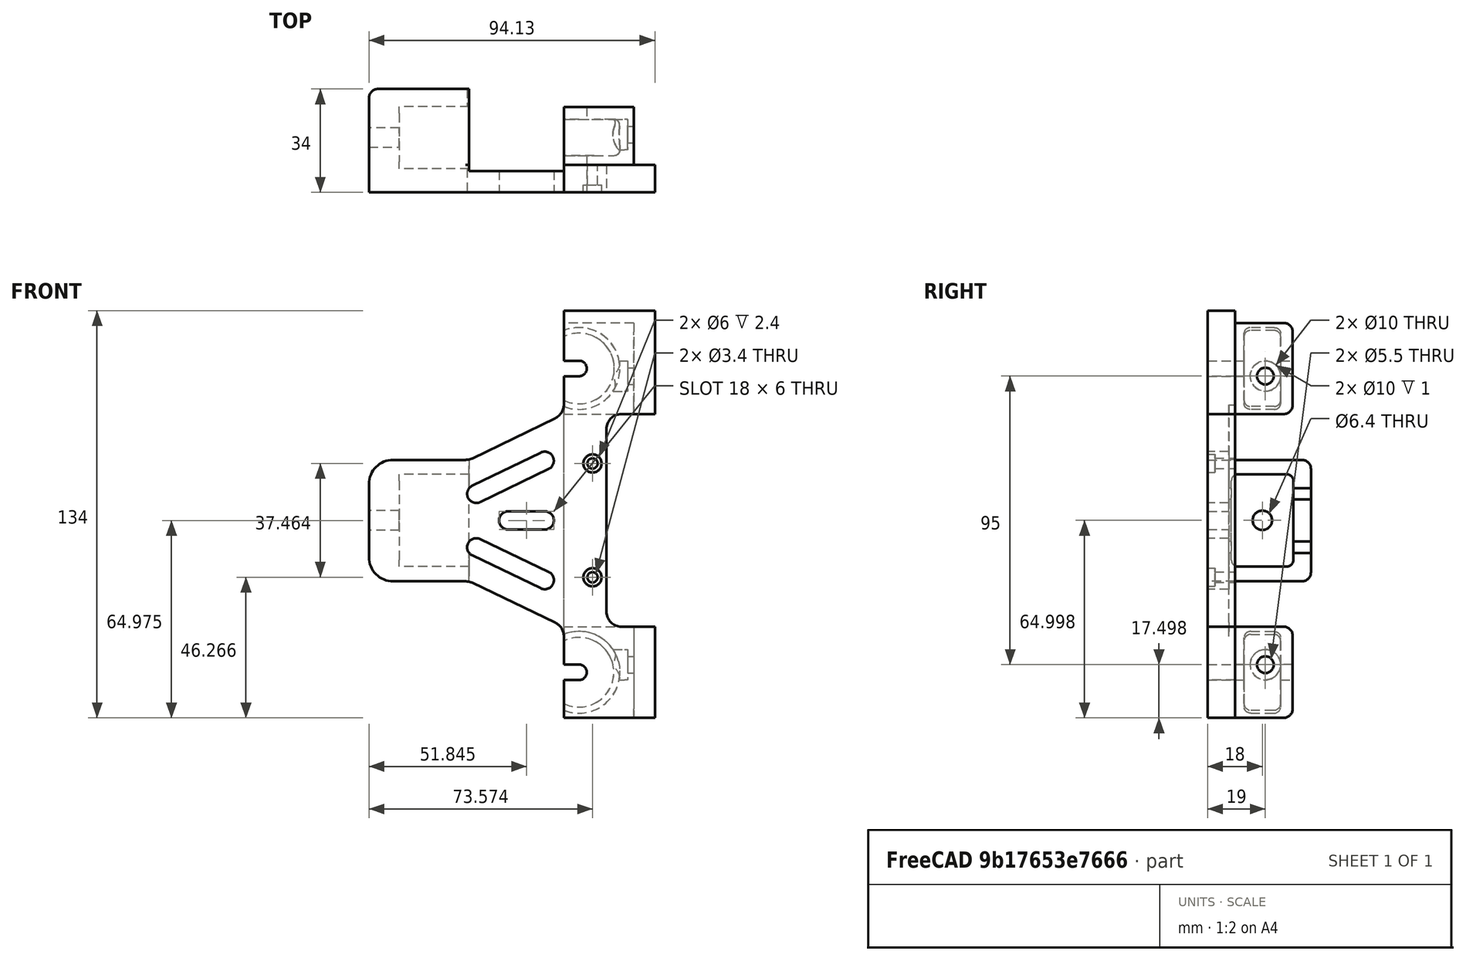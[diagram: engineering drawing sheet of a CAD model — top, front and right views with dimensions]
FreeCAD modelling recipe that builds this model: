
FCSTD DOCUMENT  (FreeCAD 0.20R29177 (Git))
Label: AQ_006a_VwheelZclamp
License: All rights reserved
LicenseURL: http://en.wikipedia.org/wiki/All_rights_reserved
objects: Sketcher::SketchObject×14, PartDesign::Pocket×9, PartDesign::Pad×5, PartDesign::Line×2, PartDesign::Groove×2, PartDesign::Hole×2, PartDesign::Fillet×2, PartDesign::SubShapeBinder×1, PartDesign::Body×1
note: 58 computed .brp shape members not serialized (recipe doc carries the construction recipe); baked Part::Feature solids carry a one-line shape summary decoded from their .brp

FEATURE [PartDesign::SubShapeBinder] Binder
  BindCopyOnChange = 0
  BindMode = 2
  ClaimChildren = false
  Context = -> Body [Binder.]
  Fuse = false
  MakeFace = true
  OffsetFill = false
  OffsetIntersection = false
  OffsetJoinType = 0
  OffsetOpenResult = false
  PartialLoad = false
  Relative = true
  _Version = 2
FEATURE [Sketcher::SketchObject] Sketch
  ExternalGeometry = -> [Binder]
  FullyConstrained = true
  MapMode = 5
  Placement = pos=(0,425,9.35e-14) rot=(1,0,0;1.5708rad)
  Support = -> [Binder]
  sketch-geometry (29):
    g0: LineSegment StartX=35.9712 StartY=288.702 StartZ=0 EndX=35.9712 EndY=315.568 EndZ=0
    g1: LineSegment StartX=35.9712 StartY=315.568 StartZ=0 EndX=58.9712 EndY=315.568 EndZ=0
    g2: LineSegment StartX=58.9712 StartY=315.568 StartZ=0 EndX=58.9712 EndY=285.568 EndZ=0
    g3: LineSegment StartX=58.9712 StartY=185.568 StartZ=0 EndX=35.9712 EndY=185.568 EndZ=0
    g4: LineSegment StartX=35.9712 StartY=185.568 StartZ=0 EndX=35.9712 EndY=212.42 EndZ=0
    g5: LineSegment StartX=58.9712 StartY=215.568 StartZ=0 EndX=58.9712 EndY=185.568 EndZ=0
    g6: LineSegment StartX=5.87245 StartY=270.987 StartZ=0 EndX=33.1511 EndY=284.202 EndZ=0
    g7: LineSegment StartX=5.86449 StartY=229.996 StartZ=0 EndX=33.1319 EndY=216.929 EndZ=0
    g8: LineSegment StartX=58.9712 StartY=285.568 StartZ=0 EndX=54.9712 EndY=285.568 EndZ=0
    g9: LineSegment StartX=49.9712 StartY=285.568 StartZ=0 EndX=35.9712 EndY=285.568 EndZ=0
    g10: LineSegment StartX=35.9712 StartY=215.568 StartZ=0 EndX=49.9712 EndY=215.568 EndZ=0
    g11: LineSegment StartX=54.9712 StartY=215.568 StartZ=0 EndX=58.9712 EndY=215.568 EndZ=0
    g12: LineSegment StartX=49.9712 StartY=280.568 StartZ=0 EndX=49.9712 EndY=220.568 EndZ=0
    g13: ArcOfCircle CenterX=54.9712 CenterY=280.568 CenterZ=0 NormalX=0 NormalY=0 NormalZ=1 AngleXU=0 Radius=5 StartAngle=1.5708 EndAngle=3.14159
    g14: GeomPoint X=49.9712 Y=285.568 Z=0
    g15: ArcOfCircle CenterX=54.9712 CenterY=220.568 CenterZ=0 NormalX=0 NormalY=0 NormalZ=1 AngleXU=0 Radius=5 StartAngle=3.14159 EndAngle=4.71239
    g16: GeomPoint X=49.9712 Y=215.568 Z=0
    g17: ArcOfCircle CenterX=30.9712 CenterY=288.702 CenterZ=0 NormalX=0 NormalY=0 NormalZ=1 AngleXU=0 Radius=5 StartAngle=5.16352 EndAngle=6.28319
    g18: GeomPoint X=35.9712 Y=285.568 Z=0
    g19: ArcOfCircle CenterX=30.9712 CenterY=212.42 CenterZ=0 NormalX=0 NormalY=0 NormalZ=1 AngleXU=0 Radius=5 StartAngle=-1.8e-15 EndAngle=1.12392
    g20: GeomPoint X=35.9712 Y=215.568 Z=0
    g21: LineSegment StartX=-28.1601 StartY=270.487 StartZ=0 EndX=3.69255 EndY=270.487 EndZ=0
    g22: LineSegment StartX=4.83989 StartY=270.487 StartZ=0 EndX=4.83989 EndY=230.487 EndZ=0
    g23: LineSegment StartX=3.70372 StartY=230.487 StartZ=0 EndX=-28.1601 EndY=230.487 EndZ=0
    g24: LineSegment StartX=-28.1601 StartY=230.487 StartZ=0 EndX=-28.1601 EndY=270.487 EndZ=0
    g25: ArcOfCircle CenterX=3.70372 CenterY=225.487 CenterZ=0 NormalX=0 NormalY=0 NormalZ=1 AngleXU=0 Radius=5 StartAngle=1.12392 EndAngle=1.5708
    g26: GeomPoint X=4.83989 Y=230.487 Z=0
    g27: ArcOfCircle CenterX=3.69255 CenterY=275.487 CenterZ=0 NormalX=0 NormalY=0 NormalZ=1 AngleXU=0 Radius=5 StartAngle=4.71239 EndAngle=5.16352
    g28: GeomPoint X=4.83989 Y=270.487 Z=0
  constraints (68):
    c: Coincident(g9,g18)
    c: Coincident(g0,g1)
    c: Coincident(g1,g2)
    c: Coincident(g2,g8)
    c: Horizontal(g1)
    c: Vertical(g0)
    c: Vertical(g2)
    c: Coincident(g8,g-4)
    c: Coincident(g0,g-3)
    c: Coincident(g3,g4)
    c: Coincident(g20,g10)
    c: Coincident(g11,g5)
    c: Coincident(g5,g3)
    c: Horizontal(g3)
    c: Vertical(g4)
    c: Vertical(g5)
    c: Coincident(g3,g-9)
    c: Coincident(g20,g-8)
    c: Coincident(g14,g9)
    c: Horizontal(g8)
    c: Horizontal(g9)
    c: Coincident(g10,g16)
    c: Horizontal(g10)
    c: Horizontal(g11)
    c: Vertical(g12)
    c: DistanceX(g14,g8) = 9
    c: PointOnObject(g14,g12)
    c: PointOnObject(g14,g8)
    c: Tangent(g12,g13) = -1.5708
    c: Tangent(g8,g13) = -1.5708
    c: PointOnObject(g16,g11)
    c: PointOnObject(g16,g12)
    c: Tangent(g11,g15) = -1.5708
    c: Tangent(g12,g15) = -1.5708
    c: PointOnObject(g18,g6)
    c: PointOnObject(g18,g0)
    c: Tangent(g6,g17) = -1.5708
    c: Tangent(g0,g17) = -1.5708
    c: PointOnObject(g20,g7)
    c: PointOnObject(g20,g4)
    c: Tangent(g7,g19) = 1.5708
    c: Tangent(g4,g19) = -1.5708
    c: Equal(g17,g19)
    c: Equal(g19,g15)
    c: Equal(g15,g13)
    c: Radius(g13) = 5
    c: Coincident(g28,g22)
    c: Coincident(g22,g26)
    c: Coincident(g23,g24)
    c: Coincident(g24,g21)
    c: Horizontal(g21)
    c: Horizontal(g23)
    c: Vertical(g22)
    c: Vertical(g24)
    c: DistanceY(g-10,g21) = 5
    c: DistanceX(g21,g-10) = 10
    c: DistanceY(g23,g-11) = 5
    c: PointOnObject(g26,g23)
    c: PointOnObject(g26,g7)
    c: Tangent(g23,g25) = -1.5708
    c: Tangent(g7,g25) = 1.5708
    c: PointOnObject(g28,g21)
    c: PointOnObject(g28,g6)
    c: Tangent(g21,g27) = -1.5708
    c: Tangent(g6,g27) = -1.5708
    c: Equal(g27,g25)
    c: Equal(g25,g19)
    c: Vertical(g22,g-10)
FEATURE [PartDesign::Pad] Pad
  Direction = (0,-1,-2e-16)
  Length = 9
  Length2 = 10
  Profile = -> Sketch
  ReferenceAxis = -> Sketch [N_Axis]
  Type = 0
FEATURE [Sketcher::SketchObject] Sketch001
  ExternalGeometry = -> [Pad,Binder]
  FullyConstrained = true
  MapMode = 5
  Placement = pos=(0,425,0) rot=(0,0.707107,0.707107;3.14159rad)
  Support = -> [Pad]
  sketch-geometry (4):
    g0: LineSegment StartX=28.1601 StartY=230.487 StartZ=0 EndX=-4.83989 EndY=230.487 EndZ=0
    g1: LineSegment StartX=-4.83989 StartY=230.487 StartZ=0 EndX=-4.83989 EndY=270.487 EndZ=0
    g2: LineSegment StartX=-4.83989 StartY=270.487 StartZ=0 EndX=28.1601 EndY=270.487 EndZ=0
    g3: LineSegment StartX=28.1601 StartY=270.487 StartZ=0 EndX=28.1601 EndY=230.487 EndZ=0
  constraints (10):
    c: Coincident(g0,g1)
    c: Coincident(g1,g2)
    c: Coincident(g2,g3)
    c: Coincident(g3,g0)
    c: Horizontal(g0)
    c: Horizontal(g2)
    c: Vertical(g1)
    c: Coincident(g0,g-3)
    c: Coincident(g2,g-3)
    c: Vertical(g1,g-4)
FEATURE [PartDesign::Pad] Pad001
  BaseFeature = -> Pad
  Direction = (0,1,-2e-16)
  Length = 25
  Length2 = 10
  Profile = -> Sketch001
  ReferenceAxis = -> Sketch001 [N_Axis]
  Type = 0
FEATURE [Sketcher::SketchObject] Sketch002
  ExternalGeometry = -> [Binder]
  FullyConstrained = true
  MapMode = 5
  Placement = pos=(4.83989,0,0) rot=(0.57735,0.57735,0.57735;2.0944rad)
  Support = -> [Pad001]
  sketch-geometry (10):
    g0: ArcOfCircle CenterX=426 CenterY=237.568 CenterZ=0 NormalX=0 NormalY=0 NormalZ=1 AngleXU=0 Radius=2.2 StartAngle=3.14159 EndAngle=4.71239
    g1: LineSegment StartX=423.8 StartY=237.568 StartZ=0 EndX=423.8 EndY=263.568 EndZ=0
    g2: ArcOfCircle CenterX=426 CenterY=263.568 CenterZ=0 NormalX=0 NormalY=0 NormalZ=1 AngleXU=0 Radius=2.2 StartAngle=1.5708 EndAngle=3.14159
    g3: LineSegment StartX=426 StartY=265.768 StartZ=0 EndX=442 EndY=265.768 EndZ=0
    g4: ArcOfCircle CenterX=442 CenterY=263.568 CenterZ=0 NormalX=0 NormalY=0 NormalZ=1 AngleXU=0 Radius=2.2 StartAngle=9e-16 EndAngle=1.5708
    g5: LineSegment StartX=444.2 StartY=263.568 StartZ=0 EndX=444.2 EndY=237.568 EndZ=0
    g6: ArcOfCircle CenterX=442 CenterY=237.568 CenterZ=0 NormalX=0 NormalY=0 NormalZ=1 AngleXU=0 Radius=2.2 StartAngle=4.71239 EndAngle=6.28319
    g7: LineSegment StartX=442 StartY=235.368 StartZ=0 EndX=426 EndY=235.368 EndZ=0
    g8: GeomPoint X=423.8 Y=235.368 Z=0
    g9: GeomPoint X=444.2 Y=265.768 Z=0
  constraints (22):
    c: Tangent(g0,g1) = 1.5708
    c: Tangent(g1,g2) = 1.5708
    c: Tangent(g2,g3) = 1.5708
    c: Tangent(g3,g4) = 1.5708
    c: Tangent(g4,g5) = 1.5708
    c: Tangent(g5,g6) = 1.5708
    c: Tangent(g6,g7) = 1.5708
    c: Tangent(g7,g0) = 1.5708
    c: Horizontal(g3)
    c: Horizontal(g7)
    c: Vertical(g1)
    c: Vertical(g5)
    c: Equal(g0,g2)
    c: Equal(g2,g4)
    c: Equal(g4,g6)
    c: PointOnObject(g8,g1)
    c: PointOnObject(g8,g7)
    c: PointOnObject(g9,g3)
    c: PointOnObject(g9,g5)
    c: Coincident(g0,g-4)
    c: Coincident(g4,g-3)
    c: DistanceX(g-3,g4) = 0.2
FEATURE [PartDesign::Pocket] Pocket
  BaseFeature = -> Pad001
  Direction = (-1,0,0)
  Length = 23
  Length2 = 5
  Profile = -> Sketch002
  ReferenceAxis = -> Sketch002 [N_Axis]
  Type = 0
FEATURE [Sketcher::SketchObject] Sketch003
  ExternalGeometry = -> [Pocket]
  FullyConstrained = true
  MapMode = 5
  Placement = pos=(-28.1601,0,0) rot=(0.57735,-0.57735,-0.57735;2.0944rad)
  Support = -> [Pocket]
  sketch-geometry (1):
    g0: Circle CenterX=-434 CenterY=250.568 CenterZ=0 NormalX=0 NormalY=0 NormalZ=1 AngleXU=0 Radius=3.2
  constraints (2):
    c: Symmetric(g-4,g-3,g0)
    c: Radius(g0) = 3.2
FEATURE [PartDesign::Pocket] Pocket001
  BaseFeature = -> Pocket
  Direction = (1,0,0)
  Length = 5
  Length2 = 5
  Profile = -> Sketch003
  ReferenceAxis = -> Sketch003 [N_Axis]
  Type = 1
FEATURE [Sketcher::SketchObject] Sketch004
  ExternalGeometry = -> [Pocket001]
  FullyConstrained = true
  MapMode = 5
  Placement = pos=(0,425,0) rot=(0,0.707107,0.707107;3.14159rad)
  Support = -> [Pocket001]
  sketch-geometry (8):
    g0: LineSegment StartX=-58.9712 StartY=315.568 StartZ=0 EndX=-35.9712 EndY=315.568 EndZ=0
    g1: LineSegment StartX=-35.9712 StartY=315.568 StartZ=0 EndX=-35.9712 EndY=285.568 EndZ=0
    g2: LineSegment StartX=-35.9712 StartY=285.568 StartZ=0 EndX=-58.9712 EndY=285.568 EndZ=0
    g3: LineSegment StartX=-58.9712 StartY=285.568 StartZ=0 EndX=-58.9712 EndY=315.568 EndZ=0
    g4: LineSegment StartX=-58.9712 StartY=185.568 StartZ=0 EndX=-35.9712 EndY=185.568 EndZ=0
    g5: LineSegment StartX=-35.9712 StartY=185.568 StartZ=0 EndX=-35.9712 EndY=215.568 EndZ=0
    g6: LineSegment StartX=-35.9712 StartY=215.568 StartZ=0 EndX=-58.9712 EndY=215.568 EndZ=0
    g7: LineSegment StartX=-58.9712 StartY=215.568 StartZ=0 EndX=-58.9712 EndY=185.568 EndZ=0
  constraints (18):
    c: Coincident(g0,g1)
    c: Coincident(g1,g2)
    c: Coincident(g2,g3)
    c: Coincident(g3,g0)
    c: Horizontal(g2)
    c: Vertical(g1)
    c: Coincident(g0,g-3)
    c: Coincident(g4,g5)
    c: Coincident(g5,g6)
    c: Coincident(g6,g7)
    c: Coincident(g7,g4)
    c: Horizontal(g6)
    c: Vertical(g5)
    c: Coincident(g4,g-4)
    c: Coincident(g4,g-6)
    c: Coincident(g6,g-4)
    c: Coincident(g2,g-3)
    c: Coincident(g0,g-5)
FEATURE [PartDesign::Pad] Pad002
  BaseFeature = -> Pocket001
  Direction = (0,1,-2e-16)
  Length = 19
  Length2 = 10
  Profile = -> Sketch004
  ReferenceAxis = -> Sketch004 [N_Axis]
  Type = 0
FEATURE [Sketcher::SketchObject] Sketch005
  ExternalGeometry = -> [Binder]
  FullyConstrained = false
  MapMode = 5
  Placement = pos=(0,416,0) rot=(1,0,0;1.5708rad)
  Support = -> [Pad002]
  sketch-geometry (8):
    g0: ArcOfCircle CenterX=40.9712 CenterY=300.568 CenterZ=0 NormalX=0 NormalY=0 NormalZ=1 AngleXU=0 Radius=2.55 StartAngle=4.71239 EndAngle=7.85398
    g1: ArcOfCircle CenterX=28.0558 CenterY=300.568 CenterZ=0 NormalX=0 NormalY=0 NormalZ=1 AngleXU=0 Radius=2.55 StartAngle=1.5708 EndAngle=4.71239
    g2: LineSegment StartX=40.9712 StartY=303.118 StartZ=0 EndX=28.0558 EndY=303.118 EndZ=0
    g3: LineSegment StartX=28.0558 StartY=298.018 StartZ=0 EndX=40.9712 EndY=298.018 EndZ=0
    g4: ArcOfCircle CenterX=40.9712 CenterY=200.568 CenterZ=0 NormalX=0 NormalY=0 NormalZ=1 AngleXU=0 Radius=2.55 StartAngle=4.71239 EndAngle=7.85398
    g5: ArcOfCircle CenterX=29.0578 CenterY=200.568 CenterZ=0 NormalX=0 NormalY=0 NormalZ=1 AngleXU=0 Radius=2.55 StartAngle=1.5708 EndAngle=4.71239
    g6: LineSegment StartX=40.9712 StartY=203.118 StartZ=0 EndX=29.0578 EndY=203.118 EndZ=0
    g7: LineSegment StartX=29.0578 StartY=198.018 StartZ=0 EndX=40.9712 EndY=198.018 EndZ=0
  constraints (16):
    c: Tangent(g0,g2) = -1.5708
    c: Tangent(g2,g1) = -1.5708
    c: Tangent(g1,g3) = -1.5708
    c: Tangent(g3,g0) = -1.5708
    c: Equal(g0,g1)
    c: Coincident(g0,g-3)
    c: Horizontal(g2)
    c: Equal(g0,g-3)
    c: Tangent(g4,g6) = -1.5708
    c: Tangent(g6,g5) = -1.5708
    c: Tangent(g5,g7) = -1.5708
    c: Tangent(g7,g4) = -1.5708
    c: Equal(g4,g5)
    c: Coincident(g4,g-4)
    c: Horizontal(g6)
    c: Equal(g4,g-4)
FEATURE [PartDesign::Pocket] Pocket002
  BaseFeature = -> Pad002
  Direction = (0,1,-2e-16)
  Length = 5
  Length2 = 5
  Profile = -> Sketch005
  ReferenceAxis = -> Sketch005 [N_Axis]
  Type = 1
FEATURE [PartDesign::Line] DatumLine
  AttacherType = Attacher::AttachEngineLine
  Length = 20
  MapMode = 19
  Placement = pos=(40.9712,416,300.568) rot=(-0.57735,-0.57735,0.57735;4.18879rad)
  ResizeMode = 0
  Support = -> [Pocket002]
FEATURE [PartDesign::Line] DatumLine001
  AttacherType = Attacher::AttachEngineLine
  Length = 20
  MapMode = 19
  Placement = pos=(40.9712,416,200.568) rot=(-0.57735,-0.57735,0.57735;4.18879rad)
  ResizeMode = 0
  Support = -> [Pocket002]
FEATURE [Sketcher::SketchObject] Sketch006
  ExternalGeometry = -> [Binder,DatumLine]
  FullyConstrained = false
  MapMode = 5
  Placement = pos=(35.9712,0,0) rot=(0.57735,-0.57735,-0.57735;2.0944rad)
  Support = -> [Pocket002]
  sketch-geometry (8):
    g0: LineSegment StartX=-428 StartY=300.568 StartZ=0 EndX=-440 EndY=300.568 EndZ=0
    g1: LineSegment StartX=-440 StartY=300.568 StartZ=0 EndX=-440 EndY=311.056 EndZ=0
    g2: LineSegment StartX=-438.001 StartY=313.054 StartZ=0 EndX=-429.999 EndY=313.054 EndZ=0
    g3: LineSegment StartX=-428 StartY=311.056 StartZ=0 EndX=-428 EndY=300.568 EndZ=0
    g4: ArcOfCircle CenterX=-438.001 CenterY=311.056 CenterZ=0 NormalX=0 NormalY=0 NormalZ=1 AngleXU=0 Radius=1.99862 StartAngle=1.5708 EndAngle=3.14159
    g5: GeomPoint X=-440 Y=313.054 Z=0
    g6: ArcOfCircle CenterX=-429.999 CenterY=311.056 CenterZ=0 NormalX=0 NormalY=0 NormalZ=1 AngleXU=0 Radius=1.99862 StartAngle=1.13e-14 EndAngle=1.5708
    g7: GeomPoint X=-428 Y=313.054 Z=0
  constraints (19):
    c: Coincident(g0,g1)
    c: Coincident(g3,g0)
    c: Horizontal(g0)
    c: Horizontal(g2)
    c: Vertical(g1)
    c: Vertical(g3)
    c: PointOnObject(g0,g-5)
    c: Horizontal(g5,g-6)
    c: Vertical(g5,g-4)
    c: Vertical(g7,g-3)
    c: PointOnObject(g5,g1)
    c: PointOnObject(g5,g2)
    c: Tangent(g1,g4) = 1.5708
    c: Tangent(g2,g4) = 1.5708
    c: PointOnObject(g7,g2)
    c: PointOnObject(g7,g3)
    c: Tangent(g2,g6) = 1.5708
    c: Tangent(g3,g6) = 1.5708
    c: Equal(g4,g6)
FEATURE [PartDesign::Groove] Groove
  Angle = 360
  Axis = (-3e-16,-1,3e-16)
  Base = (40.9712,416,300.568)
  BaseFeature = -> Pocket002
  Profile = -> Sketch006
  ReferenceAxis = -> DatumLine
  Reversed = true
FEATURE [Sketcher::SketchObject] Sketch007
  ExternalGeometry = -> [DatumLine001,Binder]
  FullyConstrained = false
  MapMode = 5
  Placement = pos=(35.9712,0,0) rot=(0.57735,-0.57735,-0.57735;2.0944rad)
  Support = -> [Groove]
  sketch-geometry (8):
    g0: LineSegment StartX=-440 StartY=200.568 StartZ=0 EndX=-428 EndY=200.568 EndZ=0
    g1: LineSegment StartX=-428 StartY=200.568 StartZ=0 EndX=-428 EndY=190.264 EndZ=0
    g2: LineSegment StartX=-430.182 StartY=188.082 StartZ=0 EndX=-437.818 EndY=188.082 EndZ=0
    g3: LineSegment StartX=-440 StartY=190.264 StartZ=0 EndX=-440 EndY=200.568 EndZ=0
    g4: ArcOfCircle CenterX=-430.182 CenterY=190.264 CenterZ=0 NormalX=0 NormalY=0 NormalZ=1 AngleXU=0 Radius=2.18218 StartAngle=4.71239 EndAngle=6.28319
    g5: GeomPoint X=-428 Y=188.082 Z=0
    g6: ArcOfCircle CenterX=-437.818 CenterY=190.264 CenterZ=0 NormalX=0 NormalY=0 NormalZ=1 AngleXU=0 Radius=2.18218 StartAngle=3.14159 EndAngle=4.71239
    g7: GeomPoint X=-440 Y=188.082 Z=0
  constraints (18):
    c: Coincident(g0,g1)
    c: Coincident(g3,g0)
    c: Horizontal(g0)
    c: Vertical(g1)
    c: Vertical(g3)
    c: PointOnObject(g0,g-3)
    c: PointOnObject(g-10,g1)
    c: PointOnObject(g-13,g3)
    c: Tangent(g2,g-11)
    c: PointOnObject(g5,g2)
    c: PointOnObject(g5,g1)
    c: Tangent(g2,g4) = 1.5708
    c: Tangent(g1,g4) = 1.5708
    c: PointOnObject(g7,g2)
    c: PointOnObject(g7,g3)
    c: Tangent(g2,g6) = 1.5708
    c: Tangent(g3,g6) = 1.5708
    c: Equal(g6,g4)
FEATURE [PartDesign::Groove] Groove001
  Angle = 360
  Axis = (-2e-16,-1,3e-16)
  Base = (40.9712,416,200.568)
  BaseFeature = -> Groove
  Profile = -> Sketch007
  ReferenceAxis = -> DatumLine001
  Reversed = true
FEATURE [Sketcher::SketchObject] Sketch008
  AttachmentOffset = pos=(0,0,-16) rot=(0,0,1;0rad)
  ExternalGeometry = -> [Binder]
  FullyConstrained = false
  MapMode = 5
  Placement = pos=(51.9712,0,0) rot=(0.57735,-0.57735,-0.57735;2.0944rad)
  Support = -> [Groove001]
  sketch-geometry (2):
    g0: Circle CenterX=-435 CenterY=203.068 CenterZ=0 NormalX=0 NormalY=0 NormalZ=1 AngleXU=0 Radius=3.5552
    g1: Circle CenterX=-435 CenterY=298.068 CenterZ=0 NormalX=0 NormalY=0 NormalZ=1 AngleXU=0 Radius=4.0073
  constraints (2):
    c: Coincident(g0,g-4)
    c: Coincident(g1,g-3)
FEATURE [Sketcher::SketchObject] Sketch009
  ExternalGeometry = -> [Groove001]
  FullyConstrained = true
  MapMode = 5
  Placement = pos=(35.9712,0,0) rot=(0.57735,-0.57735,-0.57735;2.0944rad)
  Support = -> [Groove001]
  sketch-geometry (4):
    g0: LineSegment StartX=-440 StartY=290.081 StartZ=0 EndX=-428 EndY=290.081 EndZ=0
    g1: LineSegment StartX=-428 StartY=290.081 StartZ=0 EndX=-428 EndY=311.056 EndZ=0
    g2: LineSegment StartX=-428 StartY=311.056 StartZ=0 EndX=-440 EndY=311.056 EndZ=0
    g3: LineSegment StartX=-440 StartY=311.056 StartZ=0 EndX=-440 EndY=290.081 EndZ=0
  constraints (10):
    c: Coincident(g0,g1)
    c: Coincident(g1,g2)
    c: Coincident(g2,g3)
    c: Coincident(g3,g0)
    c: Horizontal(g0)
    c: Horizontal(g2)
    c: Vertical(g1)
    c: Vertical(g3)
    c: Coincident(g0,g-4)
    c: Coincident(g1,g-3)
FEATURE [PartDesign::Pocket] Pocket003
  BaseFeature = -> Groove001
  Direction = (1,0,0)
  Length = 10
  Length2 = 5
  Profile = -> Sketch009
  ReferenceAxis = -> Sketch009 [N_Axis]
  Type = 0
FEATURE [Sketcher::SketchObject] Sketch010
  ExternalGeometry = -> [Pocket003]
  FullyConstrained = true
  MapMode = 5
  Placement = pos=(35.9712,0,0) rot=(0.57735,-0.57735,-0.57735;2.0944rad)
  Support = -> [Pocket003]
  sketch-geometry (4):
    g0: LineSegment StartX=-440 StartY=190.264 StartZ=0 EndX=-428 EndY=190.264 EndZ=0
    g1: LineSegment StartX=-428 StartY=190.264 StartZ=0 EndX=-428 EndY=210.872 EndZ=0
    g2: LineSegment StartX=-428 StartY=210.872 StartZ=0 EndX=-440 EndY=210.872 EndZ=0
    g3: LineSegment StartX=-440 StartY=210.872 StartZ=0 EndX=-440 EndY=190.264 EndZ=0
  constraints (10):
    c: Coincident(g0,g1)
    c: Coincident(g1,g2)
    c: Coincident(g2,g3)
    c: Coincident(g3,g0)
    c: Horizontal(g0)
    c: Horizontal(g2)
    c: Vertical(g1)
    c: Vertical(g3)
    c: Coincident(g0,g-4)
    c: Coincident(g1,g-3)
FEATURE [PartDesign::Pocket] Pocket004
  BaseFeature = -> Pocket003
  Direction = (1,0,0)
  Length = 10
  Length2 = 5
  Profile = -> Sketch010
  ReferenceAxis = -> Sketch010 [N_Axis]
  Type = 0
FEATURE [PartDesign::Hole] Hole
  BaseFeature = -> Pocket004
  CustomThreadClearance = 0
  Depth = 25
  DepthType = 0
  Diameter = 5.5
  DrillForDepth = false
  DrillPoint = 1
  DrillPointAngle = 118
  HoleCutCountersinkAngle = 90
  HoleCutCustomValues = false
  HoleCutDepth = 4
  HoleCutDiameter = 10
  HoleCutType = 6
  ModelThread = false
  Profile = -> Sketch008
  Tapered = false
  TaperedAngle = 90
  ThreadClass = 0
  ThreadDepth = 25
  ThreadDepthType = 0
  ThreadDirection = 0
  ThreadFit = 0
  ThreadSize = 13
  ThreadType = 1
  Threaded = false
  UseCustomThreadClearance = false
FEATURE [PartDesign::Pocket] Pocket005
  BaseFeature = -> Hole
  Direction = (1,0,0)
  Length = 1
  Length2 = 5
  Profile = -> Hole [Face101]
  Type = 0
FEATURE [PartDesign::Pocket] Pocket006
  BaseFeature = -> Pocket005
  Direction = (1,0,0)
  Length = 1
  Length2 = 5
  Profile = -> Pocket005 [Face100]
  Type = 0
FEATURE [Sketcher::SketchObject] Sketch011
  ExternalGeometry = -> [Binder]
  FullyConstrained = false
  MapMode = 5
  Placement = pos=(0,416,0) rot=(1,0,0;1.5708rad)
  Support = -> [Pocket006]
  sketch-geometry (2):
    g0: Circle CenterX=45.4137 CenterY=269.3 CenterZ=0 NormalX=0 NormalY=0 NormalZ=1 AngleXU=0 Radius=4.58581
    g1: Circle CenterX=45.4137 CenterY=231.836 CenterZ=0 NormalX=0 NormalY=0 NormalZ=1 AngleXU=0 Radius=3.59318
  constraints (2):
    c: Coincident(g0,g-3)
    c: Coincident(g1,g-4)
FEATURE [PartDesign::Hole] Hole001
  BaseFeature = -> Pocket006
  CustomThreadClearance = 0
  Depth = 25
  DepthType = 0
  Diameter = 3.4
  DrillForDepth = false
  DrillPoint = 1
  DrillPointAngle = 118
  HoleCutCountersinkAngle = 90
  HoleCutCustomValues = false
  HoleCutDepth = 2.4
  HoleCutDiameter = 6
  HoleCutType = 6
  ModelThread = false
  Profile = -> Sketch011
  Tapered = false
  TaperedAngle = 90
  ThreadClass = 0
  ThreadDepth = 25
  ThreadDepthType = 0
  ThreadDirection = 0
  ThreadFit = 0
  ThreadSize = 9
  ThreadType = 1
  Threaded = false
  UseCustomThreadClearance = false
FEATURE [Sketcher::SketchObject] Sketch012
  ExternalGeometry = -> [Hole001]
  FullyConstrained = true
  MapMode = 5
  Placement = pos=(0,416,0) rot=(1,0,0;1.5708rad)
  Support = -> [Hole001]
  sketch-geometry (12):
    g0: ArcOfCircle CenterX=7.16095 CenterY=241.701 CenterZ=0 NormalX=0 NormalY=0 NormalZ=1 AngleXU=0 Radius=3 StartAngle=1.12392 EndAngle=4.26551
    g1: ArcOfCircle CenterX=29.6908 CenterY=230.904 CenterZ=0 NormalX=0 NormalY=0 NormalZ=1 AngleXU=0 Radius=3 StartAngle=4.26551 EndAngle=7.4071
    g2: LineSegment StartX=5.86449 StartY=238.996 StartZ=0 EndX=28.3943 EndY=228.199 EndZ=0
    g3: LineSegment StartX=30.9872 StartY=233.61 StartZ=0 EndX=8.45742 EndY=244.406 EndZ=0
    g4: ArcOfCircle CenterX=7.1804 CenterY=259.287 CenterZ=0 NormalX=0 NormalY=0 NormalZ=1 AngleXU=0 Radius=3 StartAngle=2.02193 EndAngle=5.16352
    g5: ArcOfCircle CenterX=29.6793 CenterY=270.186 CenterZ=0 NormalX=0 NormalY=0 NormalZ=1 AngleXU=0 Radius=3 StartAngle=5.16352 EndAngle=8.30511
    g6: LineSegment StartX=8.48834 StartY=256.587 StartZ=0 EndX=30.9872 EndY=267.487 EndZ=0
    g7: LineSegment StartX=28.3713 StartY=272.886 StartZ=0 EndX=5.87245 EndY=261.987 EndZ=0
    g8: ArcOfCircle CenterX=29.685 CenterY=250.545 CenterZ=0 NormalX=0 NormalY=0 NormalZ=1 AngleXU=0 Radius=3 StartAngle=4.71239 EndAngle=7.85398
    g9: ArcOfCircle CenterX=17.685 CenterY=250.545 CenterZ=0 NormalX=0 NormalY=0 NormalZ=1 AngleXU=0 Radius=3 StartAngle=1.5708 EndAngle=4.71239
    g10: LineSegment StartX=29.685 StartY=253.545 StartZ=0 EndX=17.685 EndY=253.545 EndZ=0
    g11: LineSegment StartX=17.685 StartY=247.545 StartZ=0 EndX=29.685 EndY=247.545 EndZ=0
  constraints (29):
    c: Tangent(g0,g2) = -1.5708
    c: Tangent(g2,g1) = -1.5708
    c: Tangent(g1,g3) = -1.5708
    c: Tangent(g3,g0) = -1.5708
    c: Equal(g0,g1)
    c: Tangent(g4,g6) = -1.5708
    c: Tangent(g6,g5) = -1.5708
    c: Tangent(g5,g7) = -1.5708
    c: Tangent(g7,g4) = -1.5708
    c: Equal(g4,g5)
    c: Equal(g0,g4)
    c: Parallel(g7,g-3)
    c: Parallel(g2,g-4)
    c: Vertical(g0,g-4)
    c: Vertical(g4,g-3)
    c: Vertical(g1,g5)
    c: DistanceY(g-4,g0) = 9
    c: DistanceY(g4,g-3) = 9
    c: Radius(g0) = 3
    c: Distance(g7) = 25
    c: Tangent(g8,g10) = -1.5708
    c: Tangent(g10,g9) = -1.5708
    c: Tangent(g9,g11) = -1.5708
    c: Tangent(g11,g8) = -1.5708
    c: Equal(g8,g9)
    c: Horizontal(g10)
    c: Equal(g8,g5)
    c: Symmetric(g1,g5,g8)
    c: DistanceX(g10,g10) = 12
FEATURE [PartDesign::Pocket] Pocket007
  BaseFeature = -> Hole001
  Direction = (0,1,-2e-16)
  Length = 5
  Length2 = 5
  Profile = -> Sketch012
  ReferenceAxis = -> Sketch012 [N_Axis]
  Type = 1
FEATURE [PartDesign::Fillet] Fillet
  Base = -> Pocket007 [Edge125,Edge87]
  BaseFeature = -> Pocket007
  Radius = 8
  SupportTransform = false
  UseAllEdges = false
FEATURE [PartDesign::Fillet] Fillet001
  Base = -> Fillet [Edge251,Edge191,Edge194,Edge265,Edge7]
  BaseFeature = -> Fillet
  Radius = 3
  SupportTransform = false
  UseAllEdges = false
FEATURE [PartDesign::Pad] Pad003
  BaseFeature = -> Fillet001
  Direction = (1,0,0)
  Length = 7
  Length2 = 10
  Profile = -> Fillet001 [Face73,Face68]
  Type = 0
FEATURE [PartDesign::Pad] Pad004
  BaseFeature = -> Pad003
  Direction = (0,-2e-16,1)
  Length = 4
  Length2 = 10
  Profile = -> Pad003 [Face72,Face112]
  Type = 0
FEATURE [Sketcher::SketchObject] Sketch013
  ExternalGeometry = -> [Pad004]
  FullyConstrained = false
  MapMode = 5
  Placement = pos=(0,425,0) rot=(0,0.707107,0.707107;3.14159rad)
  Support = -> [Pad004]
  sketch-geometry (4):
    g0: LineSegment StartX=-35.9712 StartY=288.568 StartZ=0 EndX=-4.83989 EndY=288.568 EndZ=0
    g1: LineSegment StartX=-4.83989 StartY=288.568 StartZ=0 EndX=-4.83989 EndY=207.933 EndZ=0
    g2: LineSegment StartX=-4.83989 StartY=207.933 StartZ=0 EndX=-35.9712 EndY=207.933 EndZ=0
    g3: LineSegment StartX=-35.9712 StartY=207.933 StartZ=0 EndX=-35.9712 EndY=288.568 EndZ=0
  constraints (10):
    c: Coincident(g0,g1)
    c: Coincident(g1,g2)
    c: Coincident(g2,g3)
    c: Coincident(g3,g0)
    c: Horizontal(g0)
    c: Horizontal(g2)
    c: Vertical(g1)
    c: Vertical(g3)
    c: Coincident(g0,g-4)
    c: Vertical(g0,g-3)
FEATURE [PartDesign::Pocket] Pocket008
  BaseFeature = -> Pad004
  Direction = (0,-1,2e-16)
  Length = 2
  Length2 = 5
  Profile = -> Sketch013
  ReferenceAxis = -> Sketch013 [N_Axis]
  Type = 0
FEATURE [PartDesign::Body] Body
  Group = -> [Binder,Sketch,Pad,Sketch001,Pad001,Sketch002,Pocket,Sketch003,Pocket001,Sketch004,Pad002,Sketch005,Pocket002,DatumLine,DatumLine001,Sketch006,Groove,Sketch007,Groove001,Sketch008,Sketch009,Pocket003,Sketch010,Pocket004,Hole,Pocket005,Pocket006,Sketch011,Hole001,Sketch012,Pocket007,Fillet,Fillet001,Pad003,Pad004,Sketch013,Pocket008]
  Origin = -> Origin
  Tip = -> Pocket008
